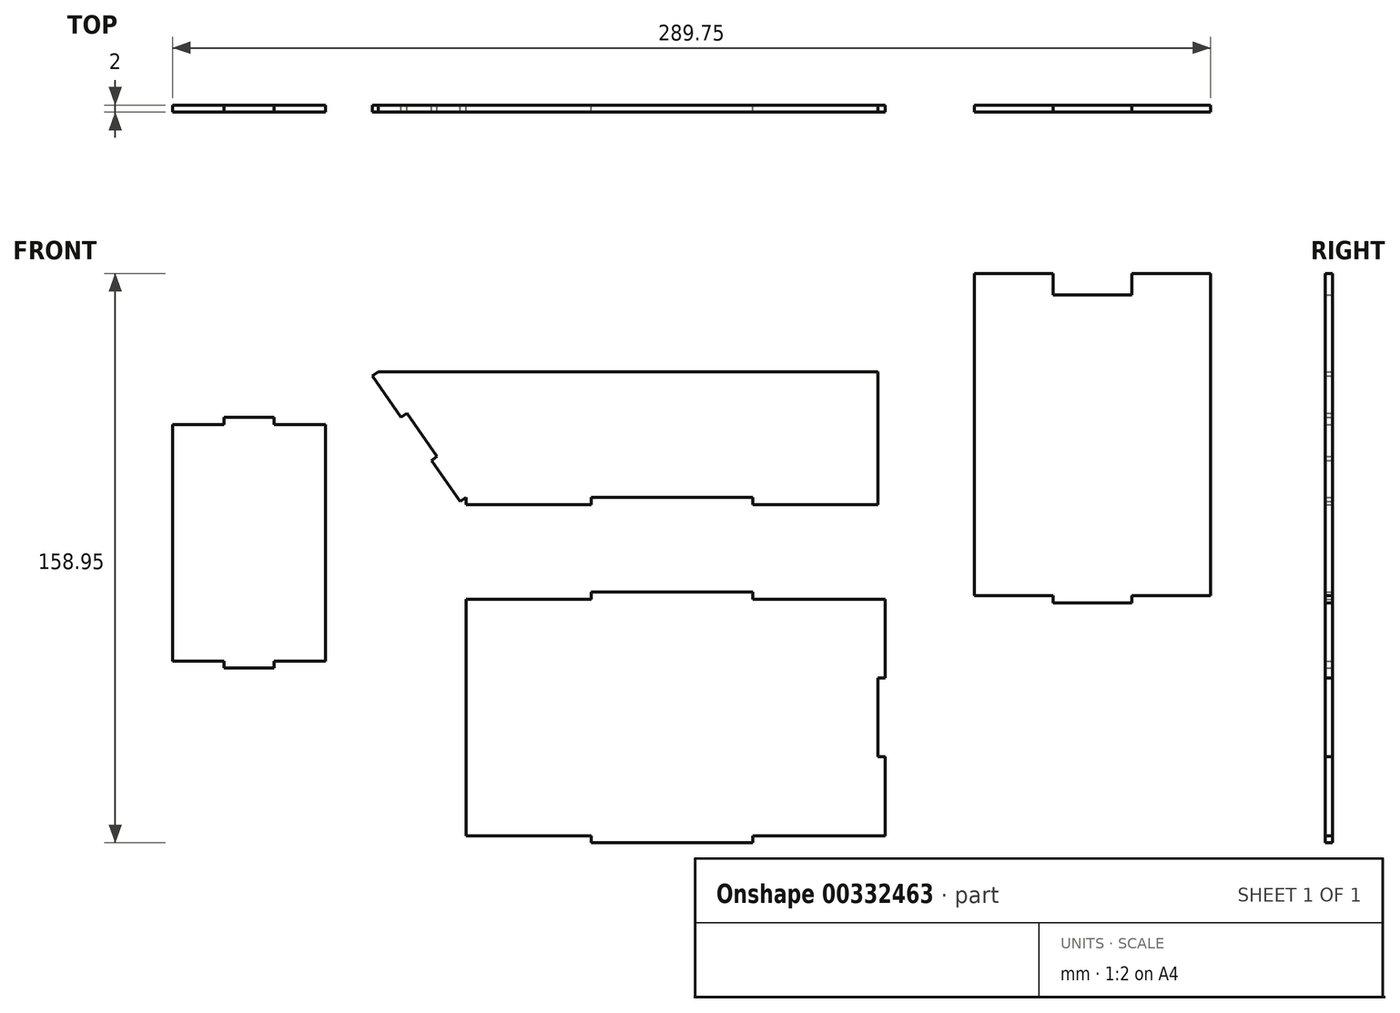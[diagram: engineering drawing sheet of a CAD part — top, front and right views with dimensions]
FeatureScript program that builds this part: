
annotation { "Feature Type Name" : "Feature", "Feature Type Description" : "" }
export const myFeature = defineFeature(function(context is Context, id is Id, definition is map)
    precondition{}
    {
        {
            var Q0;
            Q0=qCreatedBy(makeId("Front.planeOp"),FACE);
            var sketch = newSketch(context, id + "F0", { "sketchPlane" : qUnion([Q0])});
            skLineSegment(sketch, "E0.bottom", {"start": v(57.5, -17.5) * mm, "end": v(-57.5, -17.5) * mm});
            skLineSegment(sketch, "E0.top", {"start": v(57.5, 17.5) * mm, "end": v(-57.5, 17.5) * mm});
            skLineSegment(sketch, "E0.left", {"start": v(57.5, -17.5) * mm, "end": v(57.5, 17.5) * mm});
            skLineSegment(sketch, "E0.right", {"start": v(-57.5, -17.5) * mm, "end": v(-57.5, 17.5) * mm});
            skPoint(sketch, "E0.middle", {"position": v(0, 0) * mm});
            skLineSegment(sketch, "E1", {"start": v(-57.5, -17.5) * mm, "end": v(-82, 17.5) * mm});
            skLineSegment(sketch, "E2", {"start": v(-82, 17.5) * mm, "end": v(-57.5, 17.5) * mm});
            skLineSegment(sketch, "E3.bottom", {"start": v(57.5, -111.95) * mm, "end": v(-57.5, -111.95) * mm});
            skLineSegment(sketch, "E3.top", {"start": v(57.5, -45.95) * mm, "end": v(-57.5, -45.95) * mm});
            skLineSegment(sketch, "E3.left", {"start": v(57.5, -111.95) * mm, "end": v(57.5, -45.95) * mm});
            skLineSegment(sketch, "E3.right", {"start": v(-57.5, -111.95) * mm, "end": v(-57.5, -45.95) * mm});
            skPoint(sketch, "E3.middle", {"position": v(0, -78.95) * mm});
            skLineSegment(sketch, "E4.bottom", {"start": v(150.36, -45) * mm, "end": v(84.36, -45) * mm});
            skLineSegment(sketch, "E4.left", {"start": v(150.36, -45) * mm, "end": v(150.36, 45) * mm});
            skLineSegment(sketch, "E4.right", {"start": v(84.36, -45) * mm, "end": v(84.36, 45) * mm});
            skPoint(sketch, "E4.middle", {"position": v(117.36, 0) * mm});
            skLineSegment(sketch, "E5", {"start": v(84.36, 45) * mm, "end": v(106.36, 45) * mm});
            skLineSegment(sketch, "E6", {"start": v(106.36, 45) * mm, "end": v(106.36, 39) * mm});
            skLineSegment(sketch, "E7", {"start": v(106.36, 39) * mm, "end": v(128.36, 39) * mm});
            skLineSegment(sketch, "E8", {"start": v(128.36, 39) * mm, "end": v(128.36, 45) * mm});
            skLineSegment(sketch, "E9", {"start": v(128.36, 45) * mm, "end": v(150.36, 45) * mm});
            skLineSegment(sketch, "E10.bottom", {"start": v(-96.66, -63.18) * mm, "end": v(-139.4, -63.18) * mm});
            skLineSegment(sketch, "E10.top", {"start": v(-96.66, 2.82) * mm, "end": v(-139.4, 2.82) * mm});
            skLineSegment(sketch, "E10.left", {"start": v(-96.66, -63.18) * mm, "end": v(-96.66, 2.82) * mm});
            skLineSegment(sketch, "E10.right", {"start": v(-139.4, -63.18) * mm, "end": v(-139.4, 2.82) * mm});
            skPoint(sketch, "E10.middle", {"position": v(-118.03, -30.18) * mm});
            skLineSegment(sketch, "E11", {"start": v(22.5, -17.5) * mm, "end": v(22.5, -19.5) * mm});
            skLineSegment(sketch, "E12", {"start": v(22.5, -19.5) * mm, "end": v(57.5, -19.5) * mm});
            skLineSegment(sketch, "E13", {"start": v(57.5, -19.5) * mm, "end": v(57.5, -17.5) * mm});
            skLineSegment(sketch, "E14", {"start": v(-22.5, -111.95) * mm, "end": v(-22.5, -113.95) * mm});
            skLineSegment(sketch, "E15", {"start": v(-22.5, -113.95) * mm, "end": v(22.5, -113.95) * mm});
            skLineSegment(sketch, "E16", {"start": v(22.5, -113.95) * mm, "end": v(22.5, -111.95) * mm});
            skLineSegment(sketch, "E17", {"start": v(57.5, -45.95) * mm, "end": v(59.5, -45.95) * mm});
            skLineSegment(sketch, "E18", {"start": v(59.5, -45.95) * mm, "end": v(59.5, -67.95) * mm});
            skLineSegment(sketch, "E19", {"start": v(59.5, -67.95) * mm, "end": v(57.5, -67.95) * mm});
            skLineSegment(sketch, "E20", {"start": v(106.36, -45) * mm, "end": v(106.36, -47) * mm});
            skLineSegment(sketch, "E21", {"start": v(106.36, -47) * mm, "end": v(128.36, -47) * mm});
            skLineSegment(sketch, "E22", {"start": v(128.36, -47) * mm, "end": v(128.36, -45) * mm});
            skLineSegment(sketch, "E23", {"start": v(84.36, -45) * mm, "end": v(106.36, -45) * mm});
            skLineSegment(sketch, "E24", {"start": v(128.36, -45) * mm, "end": v(150.36, -45) * mm});
            skLineSegment(sketch, "E25", {"start": v(106.36, -45) * mm, "end": v(128.36, -45) * mm});
            skLineSegment(sketch, "E26", {"start": v(0, -78.95) * mm, "end": v(79.2, -78.95) * mm});
            skPoint(sketch, "E26.endSnap0", {"position": v(57.5, -78.95) * mm});
            skLineSegment(sketch, "E27", {"start": v(0, 0) * mm, "end": v(0, -27.24) * mm});
            skPoint(sketch, "E27.endSnap0", {"position": v(0, -17.5) * mm});
            skLineSegment(sketch, "E28.MirrorCS", {"start": v(-22.5, -17.5) * mm, "end": v(-22.5, -19.5) * mm});
            skLineSegment(sketch, "E29.MirrorCS", {"start": v(-22.5, -19.5) * mm, "end": v(-57.5, -19.5) * mm});
            skLineSegment(sketch, "E30.MirrorCS", {"start": v(-57.5, -19.5) * mm, "end": v(-57.5, -17.5) * mm});
            skLineSegment(sketch, "E31.MirrorCS", {"start": v(59.5, -89.95) * mm, "end": v(57.5, -89.95) * mm});
            skLineSegment(sketch, "E32.MirrorCS", {"start": v(59.5, -111.95) * mm, "end": v(59.5, -89.95) * mm});
            skLineSegment(sketch, "E33.MirrorCS", {"start": v(57.5, -111.95) * mm, "end": v(59.5, -111.95) * mm});
            skLineSegment(sketch, "E34", {"start": v(0, -111.95) * mm, "end": v(0, -113.95) * mm});
            skPoint(sketch, "E34.endSnap0", {"position": v(0, -111.95) * mm});
            skLineSegment(sketch, "E35", {"start": v(-125.03, 2.82) * mm, "end": v(-125.03, 4.82) * mm});
            skLineSegment(sketch, "E36", {"start": v(-125.03, 4.82) * mm, "end": v(-111.03, 4.82) * mm});
            skLineSegment(sketch, "E37", {"start": v(-111.03, 4.82) * mm, "end": v(-111.03, 2.82) * mm});
            skLineSegment(sketch, "E38", {"start": v(-118.03, 2.82) * mm, "end": v(-118.03, 4.82) * mm});
            skLineSegment(sketch, "E39", {"start": v(-82, 17.5) * mm, "end": v(-83.65, 16.35) * mm});
            skLineSegment(sketch, "E40", {"start": v(-83.65, 16.35) * mm, "end": v(-75.62, 4.88) * mm});
            skLineSegment(sketch, "E41", {"start": v(-75.62, 4.88) * mm, "end": v(-73.98, 6.03) * mm});
            skLineSegment(sketch, "E42", {"start": v(-57.5, -17.5) * mm, "end": v(-59.14, -18.65) * mm});
            skLineSegment(sketch, "E43", {"start": v(-59.14, -18.65) * mm, "end": v(-67.17, -7.18) * mm});
            skLineSegment(sketch, "E44", {"start": v(-67.17, -7.18) * mm, "end": v(-65.53, -6.03) * mm});
            skLineSegment(sketch, "E45", {"start": v(-118.03, -30.18) * mm, "end": v(-122.14, -30.18) * mm});
            skLineSegment(sketch, "E46.MirrorCS", {"start": v(-125.03, -65.18) * mm, "end": v(-111.03, -65.18) * mm});
            skLineSegment(sketch, "E47.MirrorCS", {"start": v(-125.03, -63.18) * mm, "end": v(-125.03, -65.18) * mm});
            skLineSegment(sketch, "E48.MirrorCS", {"start": v(-111.03, -65.18) * mm, "end": v(-111.03, -63.18) * mm});
            skLineSegment(sketch, "E49.MirrorCS", {"start": v(-22.5, -43.95) * mm, "end": v(22.5, -43.95) * mm});
            skLineSegment(sketch, "E50.MirrorCS", {"start": v(-22.5, -45.95) * mm, "end": v(-22.5, -43.95) * mm});
            skLineSegment(sketch, "E51.MirrorCS", {"start": v(22.5, -43.95) * mm, "end": v(22.5, -45.95) * mm});
            skSolve(sketch);
        }
        {
            var Q0;
            Q0 = qSketchRegion(id + "F0", true);
            extrude(context, id + "F1", {"entities" : qUnion([Q0]), "depth" : 2 * mm});
        }
    });
